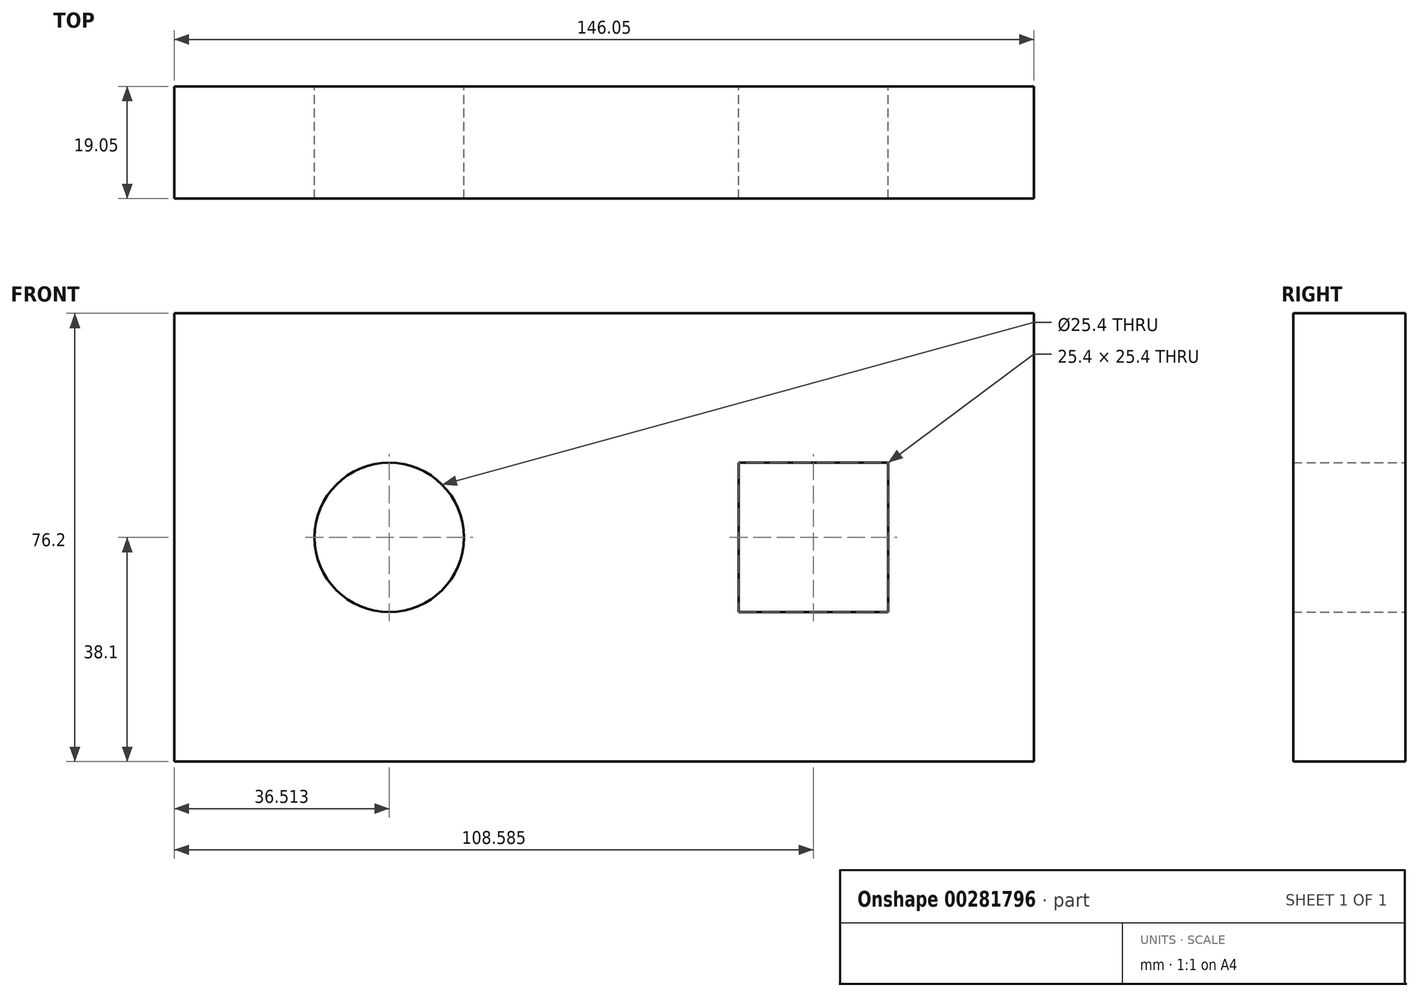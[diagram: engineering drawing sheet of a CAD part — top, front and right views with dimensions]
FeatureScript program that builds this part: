
annotation { "Feature Type Name" : "Feature", "Feature Type Description" : "" }
export const myFeature = defineFeature(function(context is Context, id is Id, definition is map)
    precondition{}
    {
        {
            var Q0;
            Q0=qCreatedBy(makeId("Front.planeOp"),FACE);
            var sketch = newSketch(context, id + "F0", { "sketchPlane" : qUnion([Q0])});
            skLineSegment(sketch, "E0.bottom", {"start": v(0, 0) * mm, "end": v(-146.05, 0) * mm});
            skLineSegment(sketch, "E0.top", {"start": v(0, 76.2) * mm, "end": v(-146.05, 76.2) * mm});
            skLineSegment(sketch, "E0.left", {"start": v(0, 0) * mm, "end": v(0, 76.2) * mm});
            skLineSegment(sketch, "E0.right", {"start": v(-146.05, 0) * mm, "end": v(-146.05, 76.2) * mm});
            skCircle(sketch, "E1", {"center": v(-109.54, 38.1) * mm, "radius": 12.7 * mm});
            skLineSegment(sketch, "E2.bottom", {"start": v(-50.17, 50.8) * mm, "end": v(-24.77, 50.8) * mm});
            skLineSegment(sketch, "E2.top", {"start": v(-50.17, 25.4) * mm, "end": v(-24.77, 25.4) * mm});
            skLineSegment(sketch, "E2.left", {"start": v(-50.17, 50.8) * mm, "end": v(-50.17, 25.4) * mm});
            skLineSegment(sketch, "E2.right", {"start": v(-24.77, 50.8) * mm, "end": v(-24.77, 25.4) * mm});
            skSolve(sketch);
        }
        {
            var Q0;
            Q0=qSketchRegion(id+"F0",true);
            extrude(context, id + "F1", {"entities" : qUnion([Q0]), "depth" : 19.05 * mm});
        }
    });
